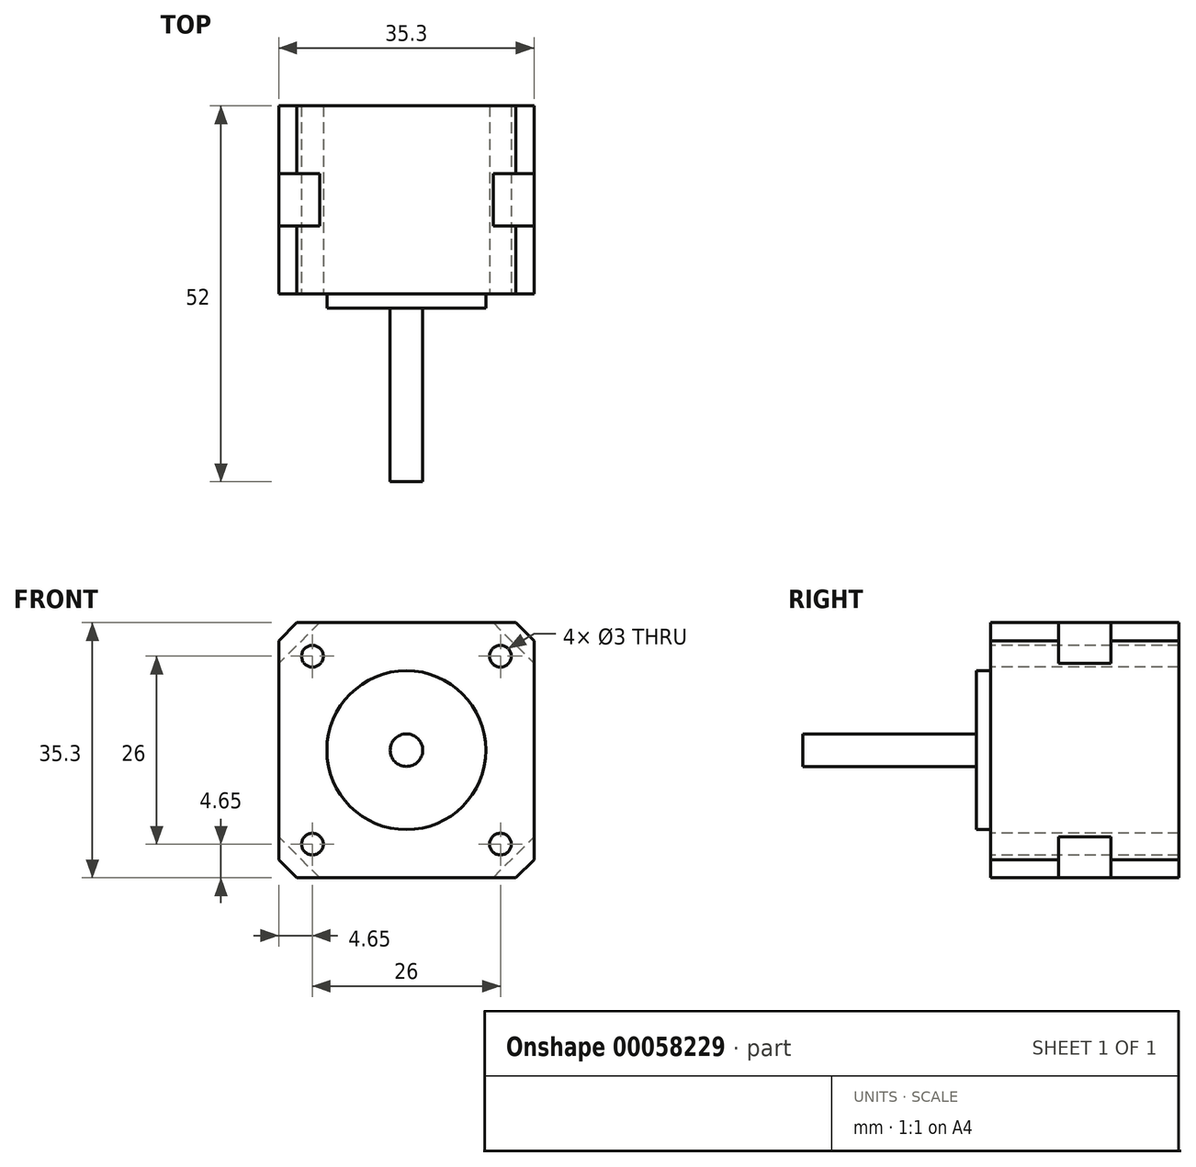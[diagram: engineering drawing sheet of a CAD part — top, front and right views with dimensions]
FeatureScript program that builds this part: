
annotation { "Feature Type Name" : "Feature", "Feature Type Description" : "" }
export const myFeature = defineFeature(function(context is Context, id is Id, definition is map)
    precondition{}
    {
        {
            var Q0;
            Q0=qCreatedBy(makeId("Front.planeOp"),FACE);
            var sketch = newSketch(context, id + "F0", { "sketchPlane" : qUnion([Q0])});
            skLineSegment(sketch, "E0.rect.bottom", {"start": v(17.65, 17.65) * mm, "end": v(-17.65, 17.65) * mm});
            skLineSegment(sketch, "E0.rect.top", {"start": v(17.65, -17.65) * mm, "end": v(-17.65, -17.65) * mm});
            skLineSegment(sketch, "E0.rect.left", {"start": v(17.65, 17.65) * mm, "end": v(17.65, -17.65) * mm});
            skLineSegment(sketch, "E0.rect.right", {"start": v(-17.65, 17.65) * mm, "end": v(-17.65, -17.65) * mm});
            skPoint(sketch, "E0.rect.middle", {"position": v(0, 0) * mm});
            skLineSegment(sketch, "E1", {"start": v(0, 17.65) * mm, "end": v(0, 0) * mm, "construction": true});
            skLineSegment(sketch, "E2", {"start": v(-17.65, 0) * mm, "end": v(0, 0) * mm, "construction": true});
            skCircle(sketch, "E3", {"center": v(13, 13) * mm, "radius": 1.5 * mm});
            skCircle(sketch, "E4.MirrorC", {"center": v(-13, 13) * mm, "radius": 1.5 * mm});
            skCircle(sketch, "E5.MirrorC", {"center": v(13, -13) * mm, "radius": 1.5 * mm});
            skCircle(sketch, "E6.MirrorC", {"center": v(-13, -13) * mm, "radius": 1.5 * mm});
            skSolve(sketch);
        }
        {
            var Q0;
            Q0 = qSketchRegion(id + "F0", true);
            extrude(context, id + "F1", {"entities" : qUnion([Q0]), "oppositeDirection" : true, "depth" : 26 * mm, "symmetric" : true});
        }
        {
            var Q0;
            Q0=makeQuery(id+"F1.opExtrude","CAP_FACE",FACE,{"disambiguationData":[OSD([sQuery(id+"F0.wireOp",EDGE,"E0.rect.bottom"),sQuery(id+"F0.wireOp",EDGE,"E0.rect.top"),sQuery(id+"F0.wireOp",EDGE,"E0.rect.left"),sQuery(id+"F0.wireOp",EDGE,"E0.rect.right"),sQuery(id+"F0.wireOp",EDGE,"E3"),sQuery(id+"F0.wireOp",EDGE,"E4.MirrorC"),sQuery(id+"F0.wireOp",EDGE,"E5.MirrorC"),sQuery(id+"F0.wireOp",EDGE,"E6.MirrorC")])],"isStart":true});
            var sketch = newSketch(context, id + "F2", { "sketchPlane" : qUnion([Q0])});
            skCircle(sketch, "E7", {"center": v(0, 0) * mm, "radius": 11 * mm});
            skSolve(sketch);
        }
        {
            var Q0;
            Q0 = qSketchRegion(id + "F2", true);
            extrude(context, id + "F3", {"entities" : qUnion([Q0]), "operationType" : NewBodyOperationType.ADD, "depth" : 2 * mm});
        }
        {
            var Q0;
            Q0=makeQuery(id+"F3.opExtrude","CAP_FACE",FACE,{"disambiguationData":[OSD([sQuery(id+"F2.wireOp",EDGE,"E7")])],"isStart":false});
            var sketch = newSketch(context, id + "F4", { "sketchPlane" : qUnion([Q0])});
            skCircle(sketch, "E8", {"center": v(0, 0) * mm, "radius": 2.25 * mm});
            skSolve(sketch);
        }
        {
            var Q0;
            Q0 = qSketchRegion(id + "F4", true);
            extrude(context, id + "F5", {"entities" : qUnion([Q0]), "operationType" : NewBodyOperationType.ADD, "depth" : 24 * mm});
        }
        {
            var Q0;
            Q0=qCreatedBy(makeId("Front.planeOp"),FACE);
            var sketch = newSketch(context, id + "F6", { "sketchPlane" : qUnion([Q0])});
            skLineSegment(sketch, "E9.0", {"start": v(17.65, 17.65) * mm, "end": v(-17.65, 17.65) * mm, "construction": true});
            skLineSegment(sketch, "E10.0", {"start": v(17.65, 17.65) * mm, "end": v(17.65, -17.65) * mm, "construction": true});
            skLineSegment(sketch, "E11", {"start": v(12, 17.65) * mm, "end": v(17.65, 12) * mm});
            skLineSegment(sketch, "E12", {"start": v(12, 17.65) * mm, "end": v(17.65, 17.65) * mm});
            skLineSegment(sketch, "E13", {"start": v(17.65, 17.65) * mm, "end": v(17.65, 12) * mm});
            skLineSegment(sketch, "E14", {"start": v(0, 17.65) * mm, "end": v(0, 0) * mm, "construction": true});
            skLineSegment(sketch, "E15", {"start": v(0, 0) * mm, "end": v(17.65, 0) * mm, "construction": true});
            skLineSegment(sketch, "E16.MirrorCS", {"start": v(17.65, -17.65) * mm, "end": v(17.65, -12) * mm});
            skLineSegment(sketch, "E17.MirrorCS", {"start": v(12, -17.65) * mm, "end": v(17.65, -17.65) * mm});
            skLineSegment(sketch, "E18.MirrorCS", {"start": v(12, -17.65) * mm, "end": v(17.65, -12) * mm});
            skLineSegment(sketch, "E19.MirrorCS", {"start": v(-17.65, -17.65) * mm, "end": v(-17.65, -12) * mm});
            skLineSegment(sketch, "E20.MirrorCS", {"start": v(-12, -17.65) * mm, "end": v(-17.65, -17.65) * mm});
            skLineSegment(sketch, "E21.MirrorCS", {"start": v(-12, -17.65) * mm, "end": v(-17.65, -12) * mm});
            skLineSegment(sketch, "E22.MirrorCS", {"start": v(-17.65, 17.65) * mm, "end": v(-17.65, 12) * mm});
            skLineSegment(sketch, "E23.MirrorCS", {"start": v(-12, 17.65) * mm, "end": v(-17.65, 17.65) * mm});
            skLineSegment(sketch, "E24.MirrorCS", {"start": v(-12, 17.65) * mm, "end": v(-17.65, 12) * mm});
            skSolve(sketch);
        }
        {
            var Q0;
            Q0 = qSketchRegion(id + "F6", true);
            extrude(context, id + "F7", {"entities" : qUnion([Q0]), "operationType" : NewBodyOperationType.REMOVE, "oppositeDirection" : true, "depth" : 7.25 * mm, "symmetric" : true});
        }
        {
            var Q0;
            {var subQ0=sQuery(id+"F0.wireOp",EDGE,"E0.rect.bottom");var subQ1=sQuery(id+"F0.wireOp",EDGE,"E0.rect.left");Q0=makeQuery(id+"F7.boolean.opBoolean","SPLIT",EDGE,{"disambiguationData":[TD([makeQuery(id+"F7.opExtrude","CAP_FACE",FACE,{"disambiguationData":[OSD([sQuery(id+"F6.wireOp",EDGE,"E11"),sQuery(id+"F6.wireOp",EDGE,"E12"),sQuery(id+"F6.wireOp",EDGE,"E13")])],"isStart":true})])],"derivedFrom":makeQuery(id+"F1.opExtrude","SWEPT_EDGE",EDGE,{"disambiguationData":[OSD([subQ0,subQ1])]})});}
            var Q1;
            {var subQ0=sQuery(id+"F0.wireOp",EDGE,"E0.rect.bottom");var subQ1=sQuery(id+"F0.wireOp",EDGE,"E0.rect.left");Q1=makeQuery(id+"F7.boolean.opBoolean","SPLIT",EDGE,{"disambiguationData":[TD([makeQuery(id+"F7.opExtrude","CAP_FACE",FACE,{"disambiguationData":[OSD([sQuery(id+"F6.wireOp",EDGE,"E11"),sQuery(id+"F6.wireOp",EDGE,"E12"),sQuery(id+"F6.wireOp",EDGE,"E13")])],"isStart":false})])],"derivedFrom":makeQuery(id+"F1.opExtrude","SWEPT_EDGE",EDGE,{"disambiguationData":[OSD([subQ0,subQ1])]})});}
            var Q2;
            {var subQ0=sQuery(id+"F0.wireOp",EDGE,"E0.rect.bottom");var subQ1=sQuery(id+"F0.wireOp",EDGE,"E0.rect.right");Q2=makeQuery(id+"F7.boolean.opBoolean","SPLIT",EDGE,{"disambiguationData":[TD([makeQuery(id+"F7.opExtrude","CAP_FACE",FACE,{"disambiguationData":[OSD([sQuery(id+"F6.wireOp",EDGE,"E22.MirrorCS"),sQuery(id+"F6.wireOp",EDGE,"E23.MirrorCS"),sQuery(id+"F6.wireOp",EDGE,"E24.MirrorCS")])],"isStart":false})])],"derivedFrom":makeQuery(id+"F1.opExtrude","SWEPT_EDGE",EDGE,{"disambiguationData":[OSD([subQ0,subQ1])]})});}
            var Q3;
            {var subQ0=sQuery(id+"F0.wireOp",EDGE,"E0.rect.bottom");var subQ1=sQuery(id+"F0.wireOp",EDGE,"E0.rect.right");Q3=makeQuery(id+"F7.boolean.opBoolean","SPLIT",EDGE,{"disambiguationData":[TD([makeQuery(id+"F7.opExtrude","CAP_FACE",FACE,{"disambiguationData":[OSD([sQuery(id+"F6.wireOp",EDGE,"E22.MirrorCS"),sQuery(id+"F6.wireOp",EDGE,"E23.MirrorCS"),sQuery(id+"F6.wireOp",EDGE,"E24.MirrorCS")])],"isStart":true})])],"derivedFrom":makeQuery(id+"F1.opExtrude","SWEPT_EDGE",EDGE,{"disambiguationData":[OSD([subQ0,subQ1])]})});}
            var Q4;
            {var subQ0=sQuery(id+"F0.wireOp",EDGE,"E0.rect.left");var subQ1=sQuery(id+"F0.wireOp",EDGE,"E0.rect.top");Q4=makeQuery(id+"F7.boolean.opBoolean","SPLIT",EDGE,{"disambiguationData":[TD([makeQuery(id+"F7.opExtrude","CAP_FACE",FACE,{"disambiguationData":[OSD([sQuery(id+"F6.wireOp",EDGE,"E16.MirrorCS"),sQuery(id+"F6.wireOp",EDGE,"E17.MirrorCS"),sQuery(id+"F6.wireOp",EDGE,"E18.MirrorCS")])],"isStart":false})])],"derivedFrom":makeQuery(id+"F1.opExtrude","SWEPT_EDGE",EDGE,{"disambiguationData":[OSD([subQ1,subQ0])]})});}
            var Q5;
            {var subQ0=sQuery(id+"F0.wireOp",EDGE,"E0.rect.left");var subQ1=sQuery(id+"F0.wireOp",EDGE,"E0.rect.top");Q5=makeQuery(id+"F7.boolean.opBoolean","SPLIT",EDGE,{"disambiguationData":[TD([makeQuery(id+"F7.opExtrude","CAP_FACE",FACE,{"disambiguationData":[OSD([sQuery(id+"F6.wireOp",EDGE,"E16.MirrorCS"),sQuery(id+"F6.wireOp",EDGE,"E17.MirrorCS"),sQuery(id+"F6.wireOp",EDGE,"E18.MirrorCS")])],"isStart":true})])],"derivedFrom":makeQuery(id+"F1.opExtrude","SWEPT_EDGE",EDGE,{"disambiguationData":[OSD([subQ1,subQ0])]})});}
            var Q6;
            {var subQ0=sQuery(id+"F0.wireOp",EDGE,"E0.rect.right");var subQ1=sQuery(id+"F0.wireOp",EDGE,"E0.rect.top");Q6=makeQuery(id+"F7.boolean.opBoolean","SPLIT",EDGE,{"disambiguationData":[TD([makeQuery(id+"F7.opExtrude","CAP_FACE",FACE,{"disambiguationData":[OSD([sQuery(id+"F6.wireOp",EDGE,"E19.MirrorCS"),sQuery(id+"F6.wireOp",EDGE,"E20.MirrorCS"),sQuery(id+"F6.wireOp",EDGE,"E21.MirrorCS")])],"isStart":true})])],"derivedFrom":makeQuery(id+"F1.opExtrude","SWEPT_EDGE",EDGE,{"disambiguationData":[OSD([subQ1,subQ0])]})});}
            var Q7;
            {var subQ0=sQuery(id+"F0.wireOp",EDGE,"E0.rect.right");var subQ1=sQuery(id+"F0.wireOp",EDGE,"E0.rect.top");Q7=makeQuery(id+"F7.boolean.opBoolean","SPLIT",EDGE,{"disambiguationData":[TD([makeQuery(id+"F7.opExtrude","CAP_FACE",FACE,{"disambiguationData":[OSD([sQuery(id+"F6.wireOp",EDGE,"E19.MirrorCS"),sQuery(id+"F6.wireOp",EDGE,"E20.MirrorCS"),sQuery(id+"F6.wireOp",EDGE,"E21.MirrorCS")])],"isStart":false})])],"derivedFrom":makeQuery(id+"F1.opExtrude","SWEPT_EDGE",EDGE,{"disambiguationData":[OSD([subQ1,subQ0])]})});}
            chamfer(context, id + "F8", {"entities" : qUnion([Q0, Q1, Q2, Q3, Q4, Q5, Q6, Q7]), "width" : 2.5 * mm, "tangentPropagation" : true});
        }
    });
